# Revit family: MDSL
name_source: partatom
category: Lighting Fixtures
units: mm (PartAtom-declared; Revit-internal decimal feet)

## family parameters
Always vertical = Yes
Cut with Voids When Loaded = No
Host = Wall
Light Source = Yes
Maintain Annotation Orientation = No
OmniClass Number = 23.80.70.00
OmniClass Title = Lighting
Part Type = Normal
Room Calculation Point = No
Round Connector Dimension = Use Diameter
Shared = No

## types (3) — shared parameters
Assembly Code = D5020200
Color Filter = 16777215
Default Elevation = 0' - 0"
Description = Wall Mounted Healthcare LED Step Light
Dimming Lamp Color Temperature Shift = <None>
Emit from Line Length = 0' - 3 1/4"
Housing Finish = Metal - Viscor - White
Lamp = LED
Length = 0' - 3 1/4"
Lens Finish = Acrylic - Viscor - Frosted Extruded Micro-Grooved
Manufacturer = CERTOLUX by VISCOR
Model = MDSL
Tilt Angle = -180.00°
URL = https://viscor.com
Voltage = 120 V
Width = 0' - 5"

## per-type parameters (varying)
| type | Apparent Load | Lamp Wattage | Photometric Web File |
| MDSLV-LED930KLS-H-UNV | 2 VA | 2 VA | MDSLV-LED930KLS-H-UNV.IES |
| MDSLV-LED930KLS-M-UNV | 1 VA | 1 VA | MDSLV-LED930KLS-M-UNV.IES |
| MDSLV-LED930KLS-L-UNV | 1 VA | 1 VA | MDSLV-LED930KLS-L-UNV.IES |

## geometry (parser evidence)
native form markers: Sweep x2
no freeform markers — native parametric forms only
